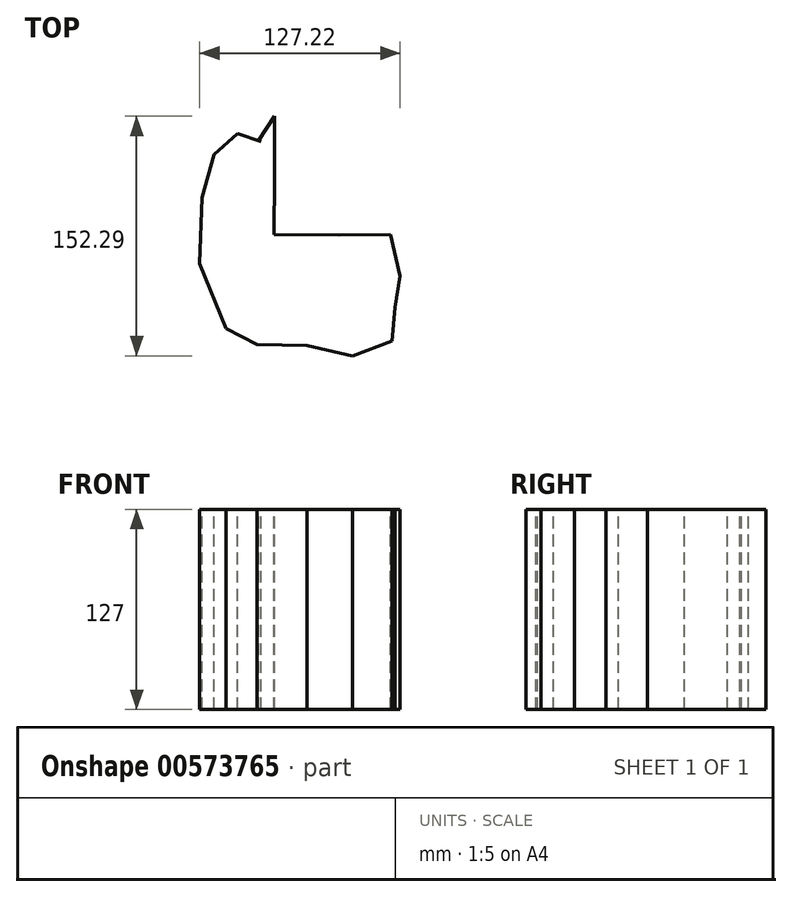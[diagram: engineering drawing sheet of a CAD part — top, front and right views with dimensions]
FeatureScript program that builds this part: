
annotation { "Feature Type Name" : "Feature", "Feature Type Description" : "" }
export const myFeature = defineFeature(function(context is Context, id is Id, definition is map)
    precondition{}
    {
        {
            var Q0;
            Q0=qCreatedBy(makeId("Top.planeOp"),FACE);
            var sketch = newSketch(context, id + "F0", { "sketchPlane" : qUnion([Q0])});
            skLineSegment(sketch, "E0", {"start": v(-10.13, 58.7) * mm, "end": v(0, 74.16) * mm});
            skLineSegment(sketch, "E1", {"start": v(0, 74.16) * mm, "end": v(0, 35.37) * mm});
            skLineSegment(sketch, "E2", {"start": v(0, 35.37) * mm, "end": v(-0.18, -1.08) * mm});
            skLineSegment(sketch, "E3", {"start": v(-0.18, -1.08) * mm, "end": v(40.96, -1.26) * mm});
            skLineSegment(sketch, "E4", {"start": v(40.96, -1.26) * mm, "end": v(73.8, -1.08) * mm});
            skLineSegment(sketch, "E5", {"start": v(73.8, -1.08) * mm, "end": v(79.76, -27.25) * mm});
            skLineSegment(sketch, "E6", {"start": v(79.76, -27.25) * mm, "end": v(76.5, -47.46) * mm});
            skLineSegment(sketch, "E7", {"start": v(76.5, -47.46) * mm, "end": v(74.52, -68.75) * mm});
            skLineSegment(sketch, "E8", {"start": v(74.52, -68.75) * mm, "end": v(49.44, -78.13) * mm});
            skLineSegment(sketch, "E9", {"start": v(49.44, -78.13) * mm, "end": v(20.57, -71.64) * mm});
            skLineSegment(sketch, "E10", {"start": v(20.57, -71.64) * mm, "end": v(-11, -70.73) * mm});
            skLineSegment(sketch, "E11", {"start": v(-11, -70.73) * mm, "end": v(-30.86, -60.63) * mm});
            skLineSegment(sketch, "E12", {"start": v(-30.86, -60.63) * mm, "end": v(-47.46, -19.3) * mm});
            skLineSegment(sketch, "E13", {"start": v(-47.46, -19.3) * mm, "end": v(-45.83, 22.56) * mm});
            skLineSegment(sketch, "E14", {"start": v(-45.83, 22.56) * mm, "end": v(-38.43, 49.8) * mm});
            skLineSegment(sketch, "E15", {"start": v(-38.43, 49.8) * mm, "end": v(-23.28, 63.16) * mm});
            skLineSegment(sketch, "E16", {"start": v(-23.28, 63.16) * mm, "end": v(-8.48, 57.92) * mm});
            skSolve(sketch);
        }
        {
            var Q0;
            Q0=sQuery(id+"F0.wireOp",EDGE,"E3");
            var Q1;
            Q1=sQuery(id+"F0.wireOp",EDGE,"E9");
            var Q2;
            Q2=sQuery(id+"F0.wireOp",EDGE,"E1");
            var Q3;
            Q3=sQuery(id+"F0.wireOp",EDGE,"E12");
            var Q4;
            Q4=sQuery(id+"F0.wireOp",EDGE,"E2");
            var Q5;
            Q5=sQuery(id+"F0.wireOp",EDGE,"E5");
            var Q6;
            Q6=sQuery(id+"F0.wireOp",EDGE,"E7");
            var Q7;
            Q7=sQuery(id+"F0.wireOp",EDGE,"E4");
            var Q8;
            Q8=sQuery(id+"F0.wireOp",EDGE,"E11");
            var Q9;
            Q9=sQuery(id+"F0.wireOp",EDGE,"E15");
            var Q10;
            Q10=sQuery(id+"F0.wireOp",EDGE,"E8");
            var Q11;
            Q11=sQuery(id+"F0.wireOp",EDGE,"E10");
            var Q12;
            Q12=sQuery(id+"F0.wireOp",EDGE,"E13");
            var Q13;
            Q13=sQuery(id+"F0.wireOp",EDGE,"E16");
            var Q14;
            Q14=sQuery(id+"F0.wireOp",EDGE,"E6");
            var Q15;
            Q15=sQuery(id+"F0.wireOp",EDGE,"E14");
            var Q16;
            Q16=sQuery(id+"F0.wireOp",EDGE,"E0");
            extrude(context, id + "F1", {"bodyType" : ToolBodyType.SURFACE, "surfaceEntities" : qUnion([Q0, Q1, Q2, Q3, Q4, Q5, Q6, Q7, Q8, Q9, Q10, Q11, Q12, Q13, Q14, Q15, Q16]), "endBound" : BoundingType.SYMMETRIC, "depth" : 127 * mm, "offsetDistance" : 25.4 * mm});
        }
    });
